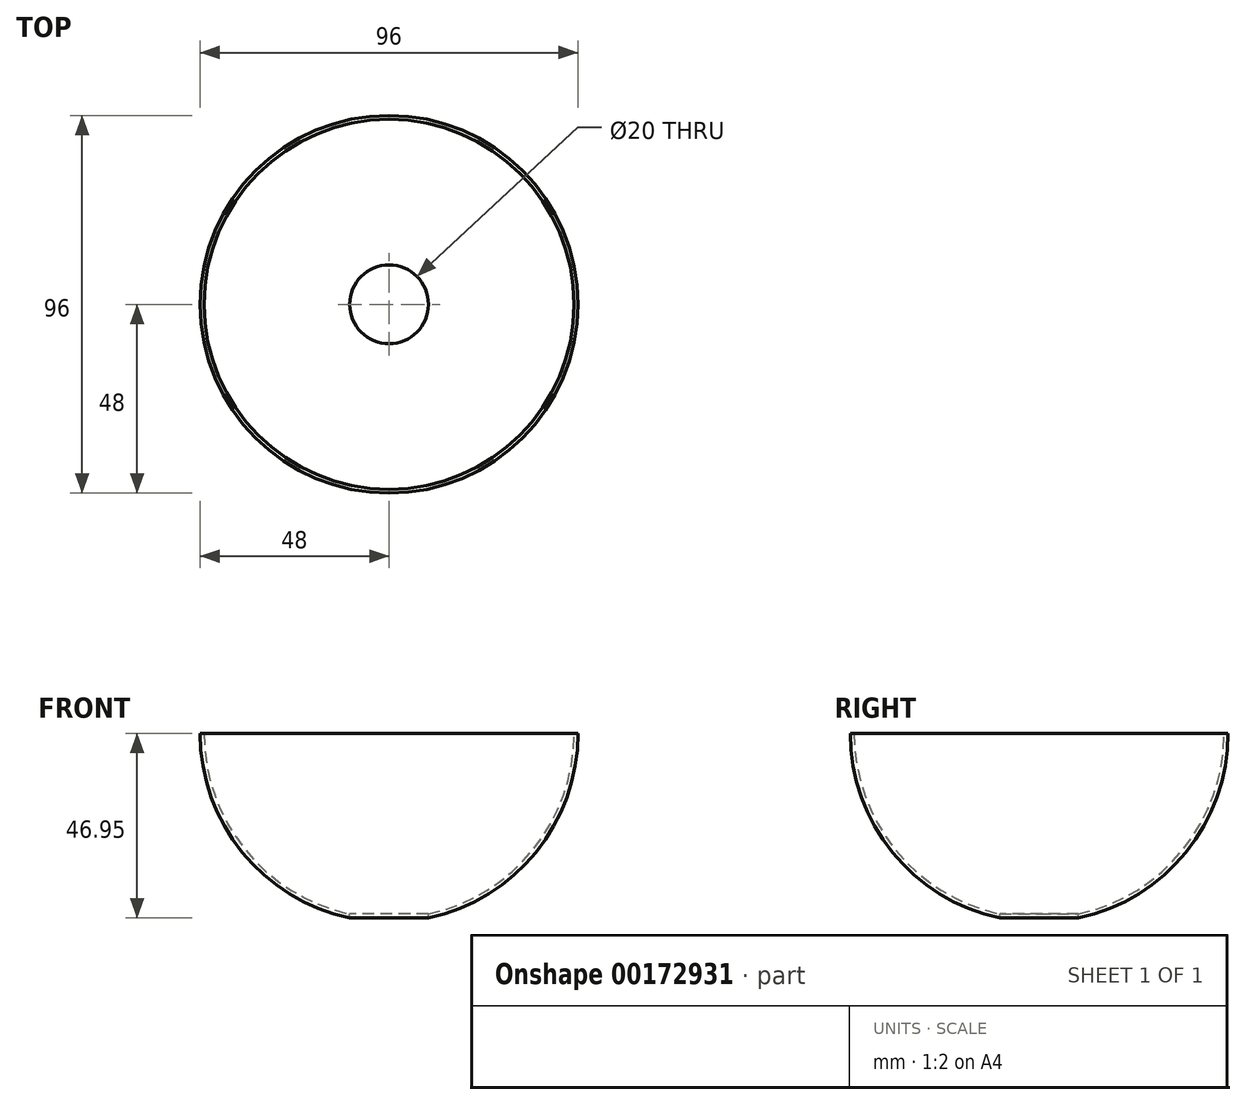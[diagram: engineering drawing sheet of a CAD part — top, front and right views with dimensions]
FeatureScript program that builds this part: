
annotation { "Feature Type Name" : "Feature", "Feature Type Description" : "" }
export const myFeature = defineFeature(function(context is Context, id is Id, definition is map)
    precondition{}
    {
        {
            var Q0;
            Q0=qCreatedBy(makeId("Top.planeOp"),FACE);
            var sketch = newSketch(context, id + "F0", { "sketchPlane" : qUnion([Q0])});
            skArc(sketch, "E0", {"start": v(0, 48) * mm, "mid": v(-48, 0) * mm, "end": v(0, -48) * mm});
            skArc(sketch, "E1", {"start": v(0, 47) * mm, "mid": v(-47, 0) * mm, "end": v(0, -47) * mm});
            skLineSegment(sketch, "E2", {"start": v(0, 48) * mm, "end": v(0, 47) * mm});
            skLineSegment(sketch, "E3.trimOffspring", {"start": v(0, -47) * mm, "end": v(0, -48) * mm});
            skSolve(sketch);
        }
        {
            var Q0;
            Q0=makeQuery(id+"F0.imprint","IMPRINT",FACE,{"disambiguationData":[TD([[makeQuery(id+"F0.imprint","IMPRINT",EDGE,{"derivedFrom":sQuery(id+"F0.wireOp",EDGE,"E0")}),1.0]])]});
            var Q1;
            Q1=sQuery(id+"F0.wireOp",EDGE,"E2");
            revolve(context, id + "F1", {"entities" : qUnion([Q0]), "axis" : qUnion([Q1]), "revolveType" : RevolveType.ONE_DIRECTION, "angle" : 180 * degree});
        }
        {
            var Q0;
            Q0=qCreatedBy(makeId("Top.planeOp"),FACE);
            var sketch = newSketch(context, id + "F2", { "sketchPlane" : qUnion([Q0])});
            skCircle(sketch, "E4", {"center": v(0, 0) * mm, "radius": 10 * mm});
            skSolve(sketch);
        }
        {
            var Q0;
            Q0=sQuery(id+"F2.wireOp",VERTEX,"E4.center");
            var Q1;
            Q1=makeQuery(id+"F1.opRevolve","SWEPT_BODY",BODY,{"disambiguationData":[OSD([sQuery(id+"F0.wireOp",EDGE,"E0"),sQuery(id+"F0.wireOp",EDGE,"E1"),sQuery(id+"F0.wireOp",EDGE,"E2"),sQuery(id+"F0.wireOp",EDGE,"E3.trimOffspring")])]});
            hole(context, id + "F3", {"style" : HoleStyle.SIMPLE, "endStyle" : HoleEndStyle.THROUGH, "holeDiameter" : 20 * mm, "startFromSketch" : true, "locations" : qUnion([Q0]), "scope" : qUnion([Q1]), "isTappedThrough" : true});
        }
    });
